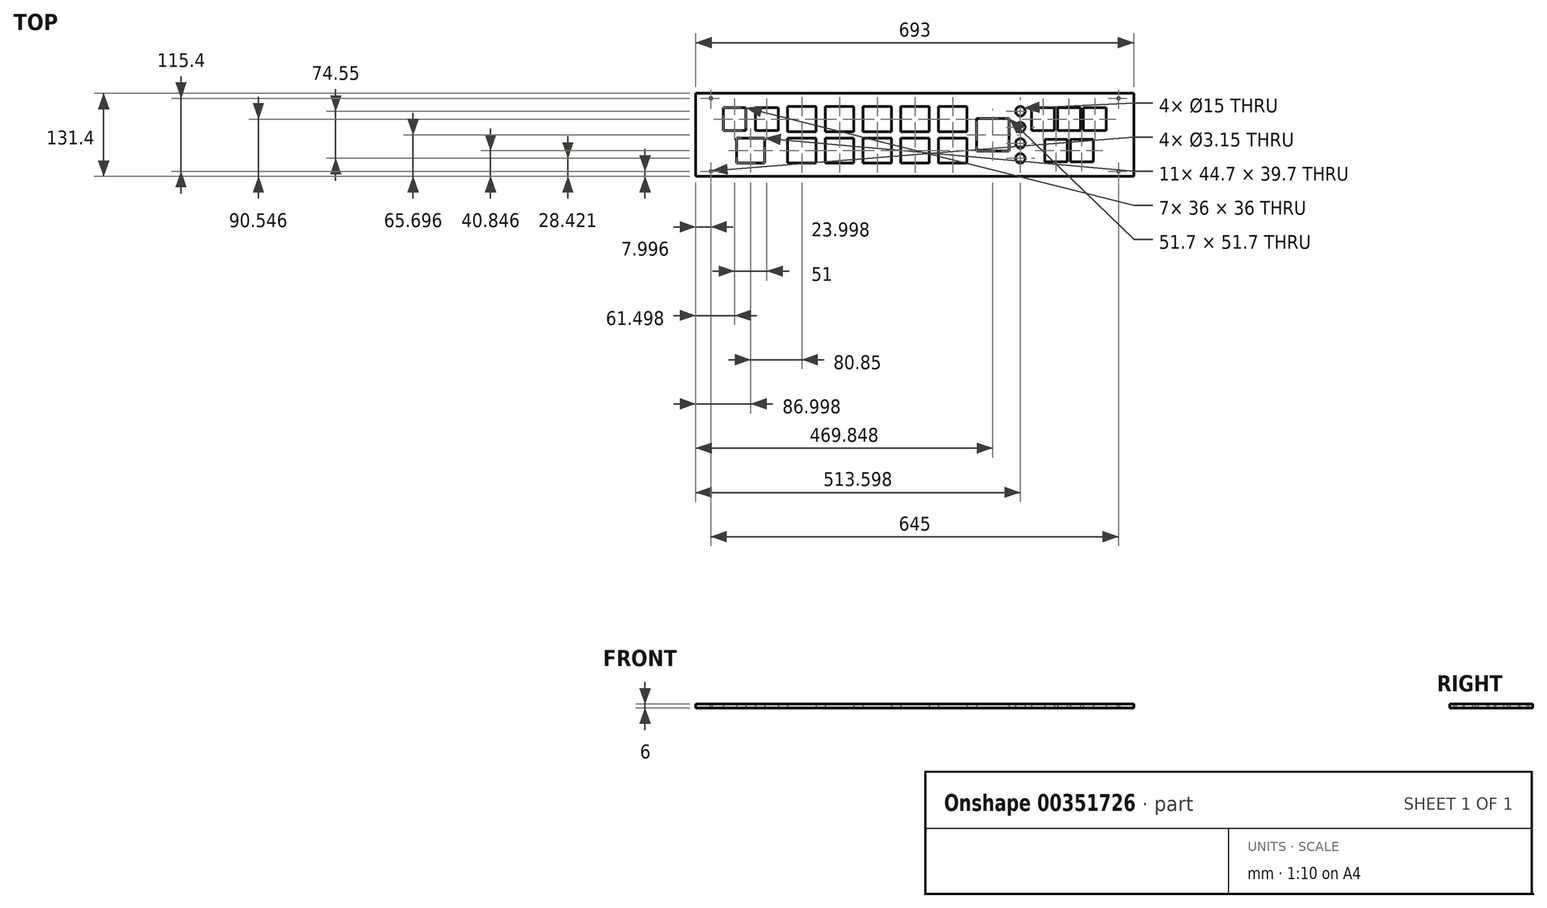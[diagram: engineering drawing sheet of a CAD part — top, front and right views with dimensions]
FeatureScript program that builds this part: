
annotation { "Feature Type Name" : "Feature", "Feature Type Description" : "" }
export const myFeature = defineFeature(function(context is Context, id is Id, definition is map)
    precondition{}
    {
        {
            var Q0;
            Q0=qCreatedBy(makeId("Top.planeOp"),FACE);
            var sketch = newSketch(context, id + "F0", { "sketchPlane" : qUnion([Q0])});
            skLineSegment(sketch, "E0.bottom", {"start": v(-604.2, 88.73) * mm, "end": v(88.8, 88.73) * mm});
            skLineSegment(sketch, "E0.top", {"start": v(-604.2, -42.67) * mm, "end": v(88.8, -42.67) * mm});
            skLineSegment(sketch, "E0.left", {"start": v(-604.2, 88.73) * mm, "end": v(-604.2, -42.67) * mm});
            skLineSegment(sketch, "E0.right", {"start": v(88.8, 88.73) * mm, "end": v(88.8, -42.67) * mm});
            skLineSegment(sketch, "E1", {"start": v(-588.2, 88.73) * mm, "end": v(-588.2, -42.67) * mm, "construction": true});
            skLineSegment(sketch, "E2", {"start": v(72.8, 88.73) * mm, "end": v(72.8, -42.67) * mm, "construction": true});
            skLineSegment(sketch, "E3", {"start": v(-604.2, 72.73) * mm, "end": v(88.8, 72.73) * mm, "construction": true});
            skLineSegment(sketch, "E4", {"start": v(-604.2, -26.67) * mm, "end": v(88.8, -26.67) * mm, "construction": true});
            skLineSegment(sketch, "E5", {"start": v(-604.2, 23.03) * mm, "end": v(88.8, 23.03) * mm, "construction": true});
            skLineSegment(sketch, "E6", {"start": v(-604.2, 47.88) * mm, "end": v(88.8, 47.88) * mm, "construction": true});
            skLineSegment(sketch, "E7", {"start": v(-604.2, -1.82) * mm, "end": v(88.8, -1.82) * mm, "construction": true});
            skLineSegment(sketch, "E8.bottom", {"start": v(-560.7, 65.88) * mm, "end": v(-524.7, 65.88) * mm});
            skLineSegment(sketch, "E8.top", {"start": v(-560.7, 29.88) * mm, "end": v(-524.7, 29.88) * mm});
            skLineSegment(sketch, "E8.left", {"start": v(-560.7, 65.88) * mm, "end": v(-560.7, 29.88) * mm});
            skLineSegment(sketch, "E8.right", {"start": v(-524.7, 65.88) * mm, "end": v(-524.7, 29.88) * mm});
            skLineSegment(sketch, "E9", {"start": v(-560.7, 65.88) * mm, "end": v(-524.7, 29.88) * mm, "construction": true});
            skLineSegment(sketch, "E10.top", {"start": v(-509.7, 29.88) * mm, "end": v(-473.7, 29.88) * mm});
            skLineSegment(sketch, "E10.left", {"start": v(-509.7, 65.88) * mm, "end": v(-509.7, 29.88) * mm});
            skLineSegment(sketch, "E10.right", {"start": v(-473.7, 65.88) * mm, "end": v(-473.7, 29.88) * mm});
            skLineSegment(sketch, "E11", {"start": v(-509.7, 65.88) * mm, "end": v(-473.7, 29.88) * mm, "construction": true});
            skLineSegment(sketch, "E12.bottom", {"start": v(-539.55, 18.03) * mm, "end": v(-494.85, 18.03) * mm});
            skLineSegment(sketch, "E12.top", {"start": v(-539.55, -21.67) * mm, "end": v(-494.85, -21.67) * mm});
            skLineSegment(sketch, "E12.left", {"start": v(-539.55, 18.03) * mm, "end": v(-539.55, -21.67) * mm});
            skLineSegment(sketch, "E12.right", {"start": v(-494.85, 18.03) * mm, "end": v(-494.85, -21.67) * mm});
            skLineSegment(sketch, "E13", {"start": v(-539.55, 18.03) * mm, "end": v(-494.85, -21.67) * mm, "construction": true});
            skLineSegment(sketch, "E14", {"start": v(-524.7, 65.88) * mm, "end": v(-509.7, 65.88) * mm, "construction": true});
            skPoint(sketch, "E15", {"position": v(-517.2, 65.88) * mm});
            skLineSegment(sketch, "E16", {"start": v(-517.2, 65.88) * mm, "end": v(-517.2, 0.68) * mm, "construction": true});
            skLineSegment(sketch, "E17.bottom", {"start": v(-458.7, 18.03) * mm, "end": v(-414, 18.03) * mm});
            skLineSegment(sketch, "E17.top", {"start": v(-458.7, -21.67) * mm, "end": v(-414, -21.67) * mm});
            skLineSegment(sketch, "E17.left", {"start": v(-458.7, 18.03) * mm, "end": v(-458.7, -21.67) * mm});
            skLineSegment(sketch, "E17.right", {"start": v(-414, 18.03) * mm, "end": v(-414, -21.67) * mm});
            skLineSegment(sketch, "E18", {"start": v(-458.7, 18.03) * mm, "end": v(-414, -21.67) * mm, "construction": true});
            skLineSegment(sketch, "E19.bottom", {"start": v(-399, 18.03) * mm, "end": v(-354.3, 18.03) * mm});
            skLineSegment(sketch, "E19.top", {"start": v(-399, -21.67) * mm, "end": v(-354.3, -21.67) * mm});
            skLineSegment(sketch, "E19.left", {"start": v(-399, 18.03) * mm, "end": v(-399, -21.67) * mm});
            skLineSegment(sketch, "E19.right", {"start": v(-354.3, 18.03) * mm, "end": v(-354.3, -21.67) * mm});
            skLineSegment(sketch, "E20", {"start": v(-399, 18.03) * mm, "end": v(-354.3, -21.67) * mm, "construction": true});
            skLineSegment(sketch, "E21.bottom", {"start": v(-339.3, 18.03) * mm, "end": v(-294.6, 18.03) * mm});
            skLineSegment(sketch, "E21.top", {"start": v(-339.3, -21.67) * mm, "end": v(-294.6, -21.67) * mm});
            skLineSegment(sketch, "E21.left", {"start": v(-339.3, 18.03) * mm, "end": v(-339.3, -21.67) * mm});
            skLineSegment(sketch, "E21.right", {"start": v(-294.6, 18.03) * mm, "end": v(-294.6, -21.67) * mm});
            skLineSegment(sketch, "E22", {"start": v(-339.3, 18.03) * mm, "end": v(-294.6, -21.67) * mm, "construction": true});
            skLineSegment(sketch, "E23.bottom", {"start": v(-279.6, 18.03) * mm, "end": v(-234.9, 18.03) * mm});
            skLineSegment(sketch, "E23.top", {"start": v(-279.6, -21.67) * mm, "end": v(-234.9, -21.67) * mm});
            skLineSegment(sketch, "E23.left", {"start": v(-279.6, 18.03) * mm, "end": v(-279.6, -21.67) * mm});
            skLineSegment(sketch, "E23.right", {"start": v(-234.9, 18.03) * mm, "end": v(-234.9, -21.67) * mm});
            skLineSegment(sketch, "E24", {"start": v(-279.6, 18.03) * mm, "end": v(-234.9, -21.67) * mm, "construction": true});
            skLineSegment(sketch, "E25.bottom", {"start": v(-219.9, 18.03) * mm, "end": v(-175.2, 18.03) * mm});
            skLineSegment(sketch, "E25.top", {"start": v(-219.9, -21.67) * mm, "end": v(-175.2, -21.67) * mm});
            skLineSegment(sketch, "E25.left", {"start": v(-219.9, 18.03) * mm, "end": v(-219.9, -21.67) * mm});
            skLineSegment(sketch, "E25.right", {"start": v(-175.2, 18.03) * mm, "end": v(-175.2, -21.67) * mm});
            skLineSegment(sketch, "E26", {"start": v(-219.9, 18.03) * mm, "end": v(-175.2, -21.67) * mm, "construction": true});
            skLineSegment(sketch, "E27.bottom", {"start": v(-458.7, 67.73) * mm, "end": v(-414, 67.73) * mm});
            skLineSegment(sketch, "E27.top", {"start": v(-458.7, 28.03) * mm, "end": v(-414, 28.03) * mm});
            skLineSegment(sketch, "E27.left", {"start": v(-458.7, 67.73) * mm, "end": v(-458.7, 28.03) * mm});
            skLineSegment(sketch, "E27.right", {"start": v(-414, 67.73) * mm, "end": v(-414, 28.03) * mm});
            skLineSegment(sketch, "E28.bottom", {"start": v(-399, 67.73) * mm, "end": v(-354.3, 67.73) * mm});
            skLineSegment(sketch, "E28.top", {"start": v(-399, 28.03) * mm, "end": v(-354.3, 28.03) * mm});
            skLineSegment(sketch, "E28.left", {"start": v(-399, 67.73) * mm, "end": v(-399, 28.03) * mm});
            skLineSegment(sketch, "E28.right", {"start": v(-354.3, 67.73) * mm, "end": v(-354.3, 28.03) * mm});
            skLineSegment(sketch, "E29", {"start": v(-399, 67.73) * mm, "end": v(-354.3, 28.03) * mm, "construction": true});
            skLineSegment(sketch, "E30.bottom", {"start": v(-339.3, 67.73) * mm, "end": v(-294.6, 67.73) * mm});
            skLineSegment(sketch, "E30.top", {"start": v(-339.3, 28.03) * mm, "end": v(-294.6, 28.03) * mm});
            skLineSegment(sketch, "E30.left", {"start": v(-339.3, 67.73) * mm, "end": v(-339.3, 28.03) * mm});
            skLineSegment(sketch, "E30.right", {"start": v(-294.6, 67.73) * mm, "end": v(-294.6, 28.03) * mm});
            skLineSegment(sketch, "E31", {"start": v(-339.3, 67.73) * mm, "end": v(-294.6, 28.03) * mm, "construction": true});
            skLineSegment(sketch, "E32.bottom", {"start": v(-279.6, 67.73) * mm, "end": v(-234.9, 67.73) * mm});
            skLineSegment(sketch, "E32.top", {"start": v(-279.6, 28.03) * mm, "end": v(-234.9, 28.03) * mm});
            skLineSegment(sketch, "E32.left", {"start": v(-279.6, 67.73) * mm, "end": v(-279.6, 28.03) * mm});
            skLineSegment(sketch, "E32.right", {"start": v(-234.9, 67.73) * mm, "end": v(-234.9, 28.03) * mm});
            skLineSegment(sketch, "E33", {"start": v(-279.6, 67.73) * mm, "end": v(-234.9, 28.03) * mm, "construction": true});
            skLineSegment(sketch, "E34.bottom", {"start": v(-219.9, 67.73) * mm, "end": v(-175.2, 67.73) * mm});
            skLineSegment(sketch, "E34.top", {"start": v(-219.9, 28.03) * mm, "end": v(-175.2, 28.03) * mm});
            skLineSegment(sketch, "E34.left", {"start": v(-219.9, 67.73) * mm, "end": v(-219.9, 28.03) * mm});
            skLineSegment(sketch, "E34.right", {"start": v(-175.2, 67.73) * mm, "end": v(-175.2, 28.03) * mm});
            skLineSegment(sketch, "E35", {"start": v(-219.9, 67.73) * mm, "end": v(-175.2, 28.03) * mm, "construction": true});
            skLineSegment(sketch, "E36.bottom", {"start": v(-160.2, 48.88) * mm, "end": v(-108.5, 48.88) * mm});
            skLineSegment(sketch, "E36.top", {"start": v(-160.2, -2.82) * mm, "end": v(-108.5, -2.82) * mm});
            skLineSegment(sketch, "E36.left", {"start": v(-160.2, 48.88) * mm, "end": v(-160.2, -2.82) * mm});
            skLineSegment(sketch, "E36.right", {"start": v(-108.5, 48.88) * mm, "end": v(-108.5, -2.82) * mm});
            skLineSegment(sketch, "E37", {"start": v(-160.2, 48.88) * mm, "end": v(-108.5, -2.82) * mm, "construction": true});
            skLineSegment(sketch, "E38.bottom", {"start": v(9.3, 65.88) * mm, "end": v(45.3, 65.88) * mm});
            skLineSegment(sketch, "E38.top", {"start": v(9.3, 29.88) * mm, "end": v(45.3, 29.88) * mm});
            skLineSegment(sketch, "E38.left", {"start": v(9.3, 65.88) * mm, "end": v(9.3, 29.88) * mm});
            skLineSegment(sketch, "E38.right", {"start": v(45.3, 65.88) * mm, "end": v(45.3, 29.88) * mm});
            skLineSegment(sketch, "E39", {"start": v(9.3, 65.88) * mm, "end": v(45.3, 29.88) * mm, "construction": true});
            skLineSegment(sketch, "E40.bottom", {"start": v(-31.7, 65.88) * mm, "end": v(4.3, 65.88) * mm});
            skLineSegment(sketch, "E40.top", {"start": v(-31.7, 29.88) * mm, "end": v(4.3, 29.88) * mm});
            skLineSegment(sketch, "E40.left", {"start": v(-31.7, 65.88) * mm, "end": v(-31.7, 29.88) * mm});
            skLineSegment(sketch, "E40.right", {"start": v(4.3, 65.88) * mm, "end": v(4.3, 29.88) * mm});
            skLineSegment(sketch, "E41", {"start": v(-31.7, 65.88) * mm, "end": v(4.3, 29.88) * mm, "construction": true});
            skLineSegment(sketch, "E42.bottom", {"start": v(-72.7, 65.88) * mm, "end": v(-36.7, 65.88) * mm});
            skLineSegment(sketch, "E42.top", {"start": v(-72.7, 29.88) * mm, "end": v(-36.7, 29.88) * mm});
            skLineSegment(sketch, "E42.left", {"start": v(-72.7, 65.88) * mm, "end": v(-72.7, 29.88) * mm});
            skLineSegment(sketch, "E42.right", {"start": v(-36.7, 65.88) * mm, "end": v(-36.7, 29.88) * mm});
            skLineSegment(sketch, "E43", {"start": v(-72.7, 65.88) * mm, "end": v(-36.7, 29.88) * mm, "construction": true});
            skLineSegment(sketch, "E44", {"start": v(-36.7, 65.88) * mm, "end": v(-31.7, 65.88) * mm, "construction": true});
            skLineSegment(sketch, "E45", {"start": v(4.3, 65.88) * mm, "end": v(9.3, 65.88) * mm, "construction": true});
            skPoint(sketch, "E46", {"position": v(6.8, 65.88) * mm});
            skPoint(sketch, "E47", {"position": v(-34.2, 65.88) * mm});
            skLineSegment(sketch, "E48.bottom", {"start": v(-52.2, 16.18) * mm, "end": v(-16.2, 16.18) * mm});
            skLineSegment(sketch, "E48.top", {"start": v(-52.2, -19.82) * mm, "end": v(-16.2, -19.82) * mm});
            skLineSegment(sketch, "E48.left", {"start": v(-52.2, 16.18) * mm, "end": v(-52.2, -19.82) * mm});
            skLineSegment(sketch, "E48.right", {"start": v(-16.2, 16.18) * mm, "end": v(-16.2, -19.82) * mm});
            skLineSegment(sketch, "E49", {"start": v(-52.2, 16.18) * mm, "end": v(-16.2, -19.82) * mm, "construction": true});
            skLineSegment(sketch, "E50", {"start": v(-34.2, 65.88) * mm, "end": v(-34.2, -1.82) * mm, "construction": true});
            skLineSegment(sketch, "E51.bottom", {"start": v(-11.2, 16.18) * mm, "end": v(24.8, 16.18) * mm});
            skLineSegment(sketch, "E51.top", {"start": v(-11.2, -19.82) * mm, "end": v(24.8, -19.82) * mm});
            skLineSegment(sketch, "E51.left", {"start": v(-11.2, 16.18) * mm, "end": v(-11.2, -19.82) * mm});
            skLineSegment(sketch, "E51.right", {"start": v(24.8, 16.18) * mm, "end": v(24.8, -19.82) * mm});
            skLineSegment(sketch, "E52", {"start": v(-11.2, 16.18) * mm, "end": v(24.8, -19.82) * mm, "construction": true});
            skLineSegment(sketch, "E53", {"start": v(6.8, 65.88) * mm, "end": v(6.8, -1.82) * mm, "construction": true});
            skPoint(sketch, "E54", {"position": v(-90.6, 60.3) * mm});
            skPoint(sketch, "E55", {"position": v(-90.6, 35.14) * mm});
            skPoint(sketch, "E56", {"position": v(-90.6, 9.5) * mm});
            skPoint(sketch, "E57", {"position": v(-90.6, -14.25) * mm});
            skCircle(sketch, "E58", {"center": v(-90.6, 60.3) * mm, "radius": 7.5 * mm});
            skCircle(sketch, "E59", {"center": v(-90.6, 35.14) * mm, "radius": 7.5 * mm});
            skCircle(sketch, "E60", {"center": v(-90.6, 9.5) * mm, "radius": 7.5 * mm});
            skCircle(sketch, "E61", {"center": v(-90.6, -14.25) * mm, "radius": 7.5 * mm});
            skCircle(sketch, "E62", {"center": v(-580.2, 80.73) * mm, "radius": 1.57 * mm});
            skCircle(sketch, "E63", {"center": v(64.8, 80.73) * mm, "radius": 1.57 * mm});
            skCircle(sketch, "E64", {"center": v(64.8, -34.67) * mm, "radius": 1.57 * mm});
            skCircle(sketch, "E65", {"center": v(-580.2, -34.67) * mm, "radius": 1.57 * mm});
            skLineSegment(sketch, "E66", {"start": v(-580.2, 80.73) * mm, "end": v(64.8, 80.73) * mm, "construction": true});
            skLineSegment(sketch, "E67", {"start": v(64.8, 80.73) * mm, "end": v(64.8, -34.67) * mm, "construction": true});
            skLineSegment(sketch, "E68", {"start": v(64.8, -34.67) * mm, "end": v(-580.2, -34.67) * mm, "construction": true});
            skLineSegment(sketch, "E69", {"start": v(-580.2, -34.67) * mm, "end": v(-580.2, 80.73) * mm, "construction": true});
            skLineSegment(sketch, "E70", {"start": v(-458.7, 67.73) * mm, "end": v(-414, 28.03) * mm, "construction": true});
            skLineSegment(sketch, "E71", {"start": v(-509.7, 65.88) * mm, "end": v(-473.7, 65.88) * mm});
            skPoint(sketch, "E72", {"position": v(-542.7, 47.88) * mm});
            skPoint(sketch, "E73", {"position": v(-491.7, 47.88) * mm});
            skPoint(sketch, "E74", {"position": v(-436.35, 47.88) * mm});
            skPoint(sketch, "E75", {"position": v(-376.65, 47.88) * mm});
            skPoint(sketch, "E76", {"position": v(-436.35, -1.82) * mm});
            skPoint(sketch, "E77", {"position": v(-376.65, -1.82) * mm});
            skPoint(sketch, "E78", {"position": v(-316.95, -1.82) * mm});
            skPoint(sketch, "E79", {"position": v(-197.55, -1.82) * mm});
            skPoint(sketch, "E80", {"position": v(-197.55, 47.88) * mm});
            skPoint(sketch, "E81", {"position": v(-316.95, 47.88) * mm});
            skPoint(sketch, "E82", {"position": v(-257.25, 47.88) * mm});
            skPoint(sketch, "E83", {"position": v(-517.2, -1.82) * mm});
            skPoint(sketch, "E84", {"position": v(-257.25, -1.82) * mm});
            skPoint(sketch, "E85", {"position": v(-134.35, 23.03) * mm});
            skPoint(sketch, "E86", {"position": v(-54.7, 47.88) * mm});
            skPoint(sketch, "E87", {"position": v(-13.7, 47.88) * mm});
            skPoint(sketch, "E88", {"position": v(27.3, 47.88) * mm});
            skPoint(sketch, "E89", {"position": v(6.8, -1.82) * mm});
            skPoint(sketch, "E90", {"position": v(-34.2, -1.82) * mm});
            skLineSegment(sketch, "E91", {"start": v(-436.35, 47.88) * mm, "end": v(-436.35, -1.82) * mm, "construction": true});
            skLineSegment(sketch, "E92", {"start": v(-376.65, 47.88) * mm, "end": v(-376.65, -1.82) * mm, "construction": true});
            skLineSegment(sketch, "E93", {"start": v(-316.95, -1.82) * mm, "end": v(-316.95, 47.88) * mm, "construction": true});
            skLineSegment(sketch, "E94", {"start": v(-257.25, 47.88) * mm, "end": v(-257.25, -1.82) * mm, "construction": true});
            skLineSegment(sketch, "E95", {"start": v(-197.55, 47.88) * mm, "end": v(-197.55, -1.82) * mm, "construction": true});
            skLineSegment(sketch, "E96", {"start": v(-72.7, 65.88) * mm, "end": v(-108.5, 65.88) * mm, "construction": true});
            skLineSegment(sketch, "E97", {"start": v(-108.5, 65.88) * mm, "end": v(-108.5, 48.88) * mm, "construction": true});
            skPoint(sketch, "E98", {"position": v(-90.6, 65.88) * mm});
            skLineSegment(sketch, "E99", {"start": v(-90.6, 65.88) * mm, "end": v(-90.6, -14.25) * mm, "construction": true});
            skSolve(sketch);
        }
        {
            var Q0;
            Q0=makeQuery(id+"F0.imprint","IMPRINT",FACE,{"disambiguationData":[TD([[makeQuery(id+"F0.imprint","IMPRINT",EDGE,{"derivedFrom":sQuery(id+"F0.wireOp",EDGE,"E0.bottom")}),-1.0]])]});
            extrude(context, id + "F1", {"entities" : qUnion([Q0]), "depth" : 6 * mm});
        }
    });
